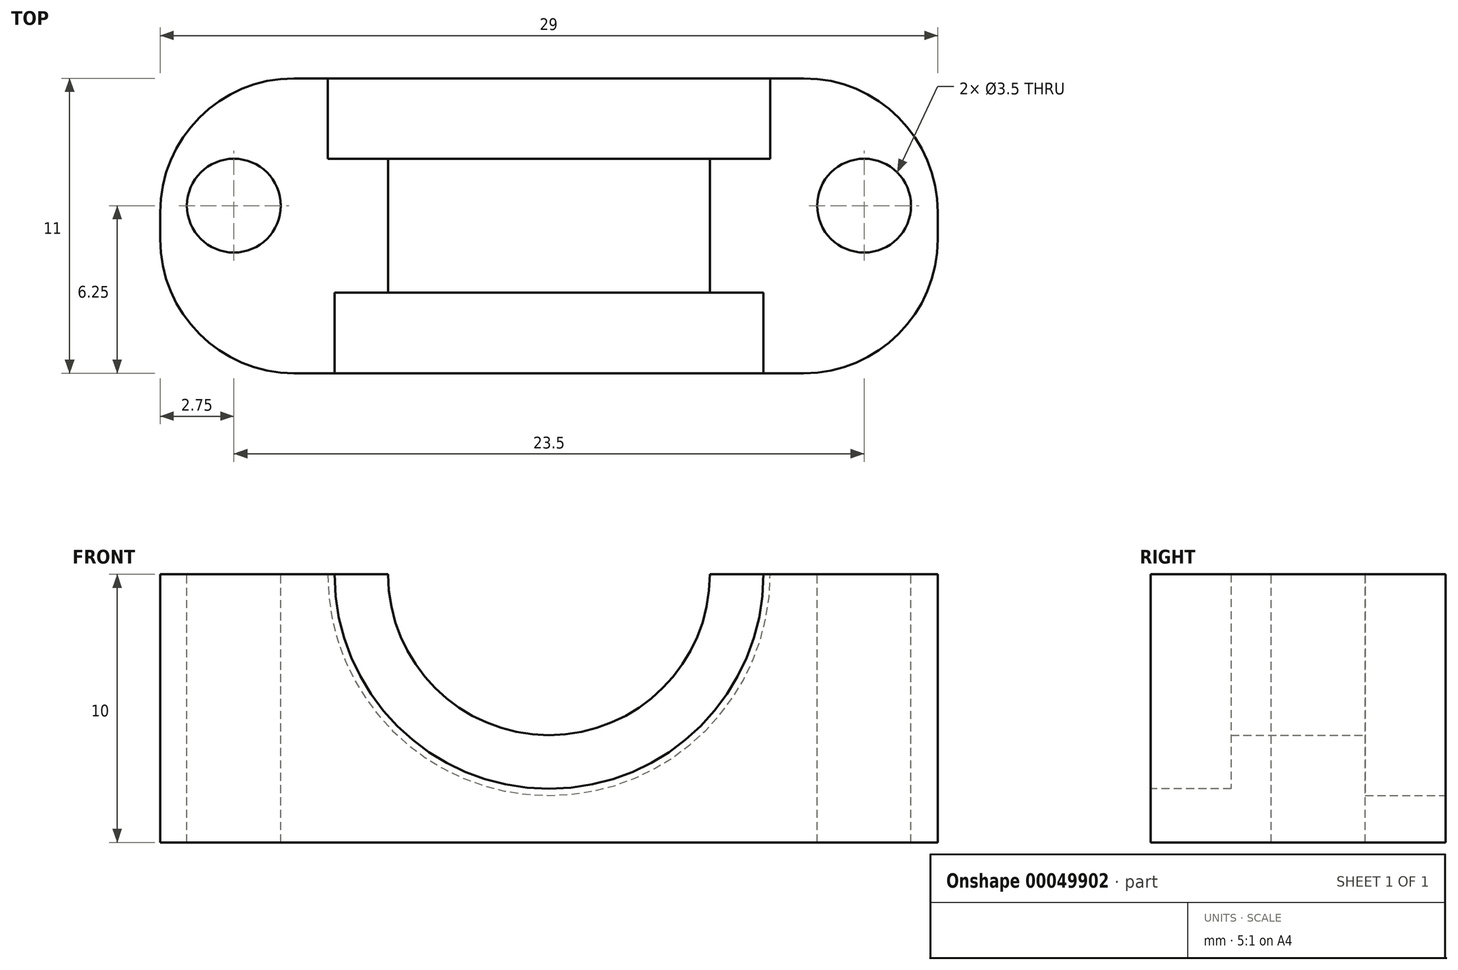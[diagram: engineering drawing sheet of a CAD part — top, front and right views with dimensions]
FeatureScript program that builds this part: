
annotation { "Feature Type Name" : "Feature", "Feature Type Description" : "" }
export const myFeature = defineFeature(function(context is Context, id is Id, definition is map)
    precondition{}
    {
        {
            var Q0;
            Q0=qCreatedBy(makeId("Top.planeOp"),FACE);
            var sketch = newSketch(context, id + "F0", { "sketchPlane" : qUnion([Q0])});
            skLineSegment(sketch, "E0.bottom", {"start": v(0, 0) * mm, "end": v(25, 0) * mm});
            skLineSegment(sketch, "E0.top", {"start": v(0, 11) * mm, "end": v(25, 11) * mm});
            skLineSegment(sketch, "E0.left", {"start": v(0, 0) * mm, "end": v(0, 11) * mm});
            skLineSegment(sketch, "E0.right", {"start": v(25, 0) * mm, "end": v(25, 11) * mm});
            skSolve(sketch);
        }
        {
            var Q0;
            Q0=qSketchRegion(id+"F0",true);
            extrude(context, id + "F1", {"entities" : qUnion([Q0]), "depth" : 10 * mm});
        }
        {
            var Q0;
            Q0=makeQuery(id+"F1.opExtrude","SWEPT_FACE",FACE,{"disambiguationData":[OSD([sQuery(id+"F0.wireOp",EDGE,"E0.bottom")])]});
            var sketch = newSketch(context, id + "F2", { "sketchPlane" : qUnion([Q0])});
            skCircle(sketch, "E1", {"center": v(12.5, 10) * mm, "radius": 8 * mm});
            skSolve(sketch);
        }
        {
            var Q0;
            Q0=qSketchRegion(id+"F2",true);
            extrude(context, id + "F3", {"entities" : qUnion([Q0]), "operationType" : NewBodyOperationType.REMOVE, "oppositeDirection" : true, "depth" : 3 * mm});
        }
        {
            var Q0;
            Q0=makeQuery(id+"F1.opExtrude","SWEPT_FACE",FACE,{"disambiguationData":[OSD([sQuery(id+"F0.wireOp",EDGE,"E0.top")])]});
            var sketch = newSketch(context, id + "F4", { "sketchPlane" : qUnion([Q0])});
            skCircle(sketch, "E2", {"center": v(-12.5, 10) * mm, "radius": 6 * mm});
            skSolve(sketch);
        }
        {
            var Q0;
            Q0=qSketchRegion(id+"F4",true);
            extrude(context, id + "F5", {"entities" : qUnion([Q0]), "operationType" : NewBodyOperationType.REMOVE, "oppositeDirection" : true, "depth" : 9 * mm});
        }
        {
            var Q0;
            Q0=makeQuery(id+"F1.opExtrude","SWEPT_FACE",FACE,{"disambiguationData":[OSD([sQuery(id+"F0.wireOp",EDGE,"E0.left")])]});
            var sketch = newSketch(context, id + "F6", { "sketchPlane" : qUnion([Q0])});
            skLineSegment(sketch, "E3.bottom", {"start": v(-11, 0) * mm, "end": v(0, 0) * mm});
            skLineSegment(sketch, "E3.top", {"start": v(-11, 10) * mm, "end": v(0, 10) * mm});
            skLineSegment(sketch, "E3.left", {"start": v(-11, 0) * mm, "end": v(-11, 10) * mm});
            skLineSegment(sketch, "E3.right", {"start": v(0, 0) * mm, "end": v(0, 10) * mm});
            skSolve(sketch);
        }
        {
            var Q0;
            Q0=qSketchRegion(id+"F6",true);
            extrude(context, id + "F7", {"entities" : qUnion([Q0]), "operationType" : NewBodyOperationType.ADD, "depth" : 2 * mm});
        }
        {
            var Q0;
            Q0=makeQuery(id+"F1.opExtrude","SWEPT_FACE",FACE,{"disambiguationData":[OSD([sQuery(id+"F0.wireOp",EDGE,"E0.right")])]});
            var sketch = newSketch(context, id + "F8", { "sketchPlane" : qUnion([Q0])});
            skLineSegment(sketch, "E4.bottom", {"start": v(11, 10) * mm, "end": v(0, 10) * mm});
            skLineSegment(sketch, "E4.top", {"start": v(11, 0) * mm, "end": v(0, 0) * mm});
            skLineSegment(sketch, "E4.left", {"start": v(11, 10) * mm, "end": v(11, 0) * mm});
            skLineSegment(sketch, "E4.right", {"start": v(0, 10) * mm, "end": v(0, 0) * mm});
            skSolve(sketch);
        }
        {
            var Q0;
            Q0=qSketchRegion(id+"F8",true);
            extrude(context, id + "F9", {"entities" : qUnion([Q0]), "operationType" : NewBodyOperationType.ADD, "depth" : 2 * mm});
        }
        {
            var Q0;
            Q0=makeQuery(id+"F9.opExtrude","CAP_EDGE",EDGE,{"disambiguationData":[OSD([sQuery(id+"F8.wireOp",EDGE,"E4.left")])],"isStart":false});
            var Q1;
            Q1=makeQuery(id+"F9.opExtrude","CAP_EDGE",EDGE,{"disambiguationData":[OSD([sQuery(id+"F8.wireOp",EDGE,"E4.right")])],"isStart":false});
            var Q2;
            Q2=makeQuery(id+"F7.opExtrude","CAP_EDGE",EDGE,{"disambiguationData":[OSD([sQuery(id+"F6.wireOp",EDGE,"E3.left")])],"isStart":false});
            var Q3;
            Q3=makeQuery(id+"F7.opExtrude","CAP_EDGE",EDGE,{"disambiguationData":[OSD([sQuery(id+"F6.wireOp",EDGE,"E3.right")])],"isStart":false});
            fillet(context, id + "F10", {"entities" : qUnion([Q0, Q1, Q2, Q3]), "radius" : 5 * mm, "tangentPropagation" : true, "allowEdgeOverflow" : false});
        }
        {
            var Q0;
            {var subQ0=sQuery(id+"F0.wireOp",EDGE,"E0.bottom");var subQ1=sQuery(id+"F0.wireOp",EDGE,"E0.top");var subQ2=sQuery(id+"F0.wireOp",EDGE,"E0.left");Q0=makeQuery(id+"F5.boolean.opBoolean","SPLIT",FACE,{"disambiguationData":[TD([makeQuery(id+"F1.opExtrude","SWEPT_FACE",FACE,{"disambiguationData":[OSD([subQ2])]})])],"derivedFrom":makeQuery(id+"F1.opExtrude","CAP_FACE",FACE,{"disambiguationData":[OSD([subQ0,subQ1,subQ2,sQuery(id+"F0.wireOp",EDGE,"E0.right")])],"isStart":false})});}
            var sketch = newSketch(context, id + "F11", { "sketchPlane" : qUnion([Q0])});
            skCircle(sketch, "E5", {"center": v(0.75, 6.25) * mm, "radius": 1.75 * mm});
            skCircle(sketch, "E6", {"center": v(24.25, 6.25) * mm, "radius": 1.75 * mm});
            skSolve(sketch);
        }
        {
            var Q0;
            Q0=qSketchRegion(id+"F11",true);
            extrude(context, id + "F12", {"entities" : qUnion([Q0]), "operationType" : NewBodyOperationType.REMOVE, "oppositeDirection" : true, "depth" : 25 * mm});
        }
        {
            var Q0;
            Q0=makeQuery(id+"F9.boolean.opBoolean","MERGE",FACE,{"derivedFrom":[makeQuery(id+"F7.boolean.opBoolean","MERGE",FACE,{"derivedFrom":[makeQuery(id+"F1.opExtrude","SWEPT_FACE",FACE,{"disambiguationData":[OSD([sQuery(id+"F0.wireOp",EDGE,"E0.top")])]}),makeQuery(id+"F7.opExtrude","SWEPT_FACE",FACE,{"disambiguationData":[OSD([sQuery(id+"F6.wireOp",EDGE,"E3.left")])]})]}),makeQuery(id+"F9.opExtrude","SWEPT_FACE",FACE,{"disambiguationData":[OSD([sQuery(id+"F8.wireOp",EDGE,"E4.left")])]})]});
            var sketch = newSketch(context, id + "F13", { "sketchPlane" : qUnion([Q0])});
            skCircle(sketch, "E7", {"center": v(-12.5, 10) * mm, "radius": 8.25 * mm});
            skSolve(sketch);
        }
        {
            var Q0;
            Q0=qSketchRegion(id+"F13",true);
            extrude(context, id + "F14", {"entities" : qUnion([Q0]), "operationType" : NewBodyOperationType.REMOVE, "oppositeDirection" : true, "depth" : 3 * mm});
        }
    });
